# Revit family: FOR UPDATE_54010CHN_NEW
name_source: partatom
category: Furniture
revit_build: Autodesk Revit 2018 (Build: 20170223_1515(x64)
units: mm (PartAtom-declared; Revit-internal decimal feet)

## family parameters
Always vertical = No
Cut with Voids When Loaded = No
OmniClass Number = 23.40.00.00
OmniClass Title = Equipment and Furnishings
Room Calculation Point = No
Shared = No
Work Plane-Based = Yes

## types (1)
- 477 Agategrey
    Always visible = Yes
    BIMobject category = Storage
    Default Elevation = 1219.2 mm  [stored 4 ft]
    Description = CubeStack Tall cabinet door hinge right 400/350
    Design country = Germany
    EAN code = 4059625328699
    Edition number = 1
    IFC Classification = Furnishing Element
    Manufacturer = hansgrohe
    Manufacturer country = Germany
    Manufacturer name = hansgrohe
    Masterformat 2014 Code = 12 35 30.23
    Masterformat 2014 Description = Bathroom Casework
    Material 1 = Hansgrohe - Wood - 477 Agategrey
    Model = 54010CHN
    NBS Reference Code = 35-75-08
    NBS Reference Description = Bathroom Cabinets
    OmniClass Code = 23-31 25 13
    OmniClass Description = Bathroom Cabinets
    Product Guid = 25f87a32-1ef0-4b39-b4ef-02402a4eaf5e
    Product SKU = 54010CHN
    Product data url = https://bimobject.com
    Product family = CubeStack
    Product group = bathroom vanity
    Product name = 54010CHN CubeStack Tall cabinet door hinge right 400/350
    QR code = https://bimobject.com
    UNSPSC Code = 30161801
    URL = https://www.hansgrohe.com
    Uniclass 2015 Code = Pr_40_30_78_03
    Uniclass 2015 Name = Bathroom cabinets
    Uniformat II Code = E2020
    Uniformat II Description = Movable Furnishings

note: [stored X ft] marks values corroborated as IEEE doubles in the binary element streams (Revit-internal decimal feet)

## geometry (parser evidence)
native form markers: Sweep x2
no freeform markers — native parametric forms only
